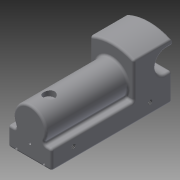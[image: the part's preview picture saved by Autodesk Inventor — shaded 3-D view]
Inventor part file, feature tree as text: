
AUTODESK INVENTOR PART (.ipt)
format: ipt  version: 2015 (Build 190159000, 159)  size: 283,136 bytes
history: native  units: in
note: dims shown in document units (in); Inventor stores cm internally (conversion verified against a paired STEP export)
features: sketch x8, extrude x5, hole x4, plane x2, mirror x1, fillet x1
ambient origin geometry x8: Origin, YZ Plane, XZ Plane, XY Plane, X Axis, Y Axis, Z Axis, Center Point
bodies: Solid1 (feature_tree)
feature tree (21):
  extrude  "Extrusion1"  Depth=1.0in
  hole  "Hole1"  [1 undecoded]
  plane  "Work Plane1"
  extrude  "Extrusion2"  Depth=0.875in
  sketch  "Sketch4"  dims[d6=3.75in d7=0.0in d8=0.375in]
  extrude  "Extrusion3"  Depth=0.375in
  extrude  "Extrusion4"  Depth=0.625in
  sketch  "Sketch8"  dims[d13=0.125in]
  hole  "Hole2"  [1 undecoded]
  hole  "Hole3"  [1 undecoded]
  sketch  "Sketch9"  dims[d14=0.125in d15=0.75in d16=0.375in d17=0.25in d18=0.5635in d19=0.125in d20=0.8108in d21=0.875in d22=0.5in d23=0.25in d24=0.0in d25=1.0in d26=0.5in d27=1.75in d28=0.0in d29=0.0in d30=4.0in d31=0.0in d32=1.0in d33=1.75in d34=0.25in d35=3.0in d36=0.0in d38=0.5in d39=1.0in d40=0.196in d41=0.875in d42=0.375in d43=0.25in d44=0.5635in d45=0.875in d46=0.8108in d47=0.196in d48=0.875in d49=0.375in d50=0.25in d51=0.5635in d52=0.875in d53=0.8108in d54=0.375in d55=1.0in d56=0.0in d57=2.35in d58=0.0in d59=3.0in d60=0.0in d61=0.25in d62=0.875in d63=0.375in d64=0.25in d65=0.5635in d66=0.5in d67=0.8108in d68=0.1in]
  extrude  "Extrusion5"  Depth=0.1in
  hole  "Hole4"  [1 undecoded]
  plane  "Work Plane2"
  mirror  "Mirror1"
  fillet  "Fillet1"  Radius=1.0in
  sketch  "Sketch1"  dims[d0=2.0in d1=1.0in]
  sketch  "Sketch2"  dims[d2=1.5in d3=0.875in]
  sketch  "Sketch3"  dims[d4=1.375in d5=0.875in]
  sketch  "Sketch6"  dims[d9=0.125in d10=0.625in]
  sketch  "Sketch7"  dims[d11=1.0in d12=0.375in]
note: 4 required parameter values undecoded (feature->parameter linkage not recoverable at this tier; creation-order binding heuristic only, values carry confidence <= 0.55)
